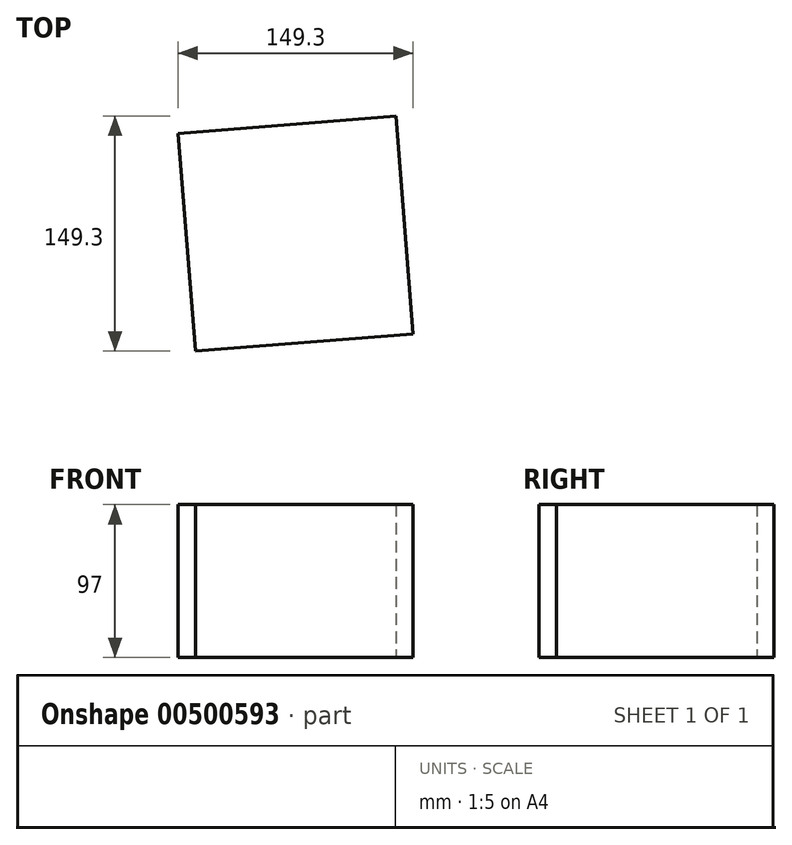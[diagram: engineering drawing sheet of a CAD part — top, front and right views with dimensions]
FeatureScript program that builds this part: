
annotation { "Feature Type Name" : "Feature", "Feature Type Description" : "" }
export const myFeature = defineFeature(function(context is Context, id is Id, definition is map)
    precondition{}
    {
        {
            var Q0;
            Q0=qCreatedBy(makeId("Top.planeOp"),FACE);
            var sketch = newSketch(context, id + "F0", { "sketchPlane" : qUnion([Q0])});
            skCircle(sketch, "E0.cCircle", {"center": v(0, 0) * mm, "radius": 98.08 * mm, "construction": true});
            skLineSegment(sketch, "E0.0", {"start": v(74.65, -63.62) * mm, "end": v(-63.62, -74.65) * mm});
            skLineSegment(sketch, "E0.1", {"start": v(-63.62, -74.65) * mm, "end": v(-74.65, 63.62) * mm});
            skLineSegment(sketch, "E0.2", {"start": v(-74.65, 63.62) * mm, "end": v(63.62, 74.65) * mm});
            skLineSegment(sketch, "E0.3", {"start": v(63.62, 74.65) * mm, "end": v(74.65, -63.62) * mm});
            skSolve(sketch);
        }
        {
            var Q0;
            Q0=makeQuery(id+"F0.imprint","IMPRINT",FACE,{"disambiguationData":[TD([[makeQuery(id+"F0.imprint","IMPRINT",EDGE,{"derivedFrom":sQuery(id+"F0.wireOp",EDGE,"E0.0")}),-1.0]])]});
            extrude(context, id + "F1", {"entities" : qUnion([Q0]), "depth" : 97 * mm});
        }
    });
